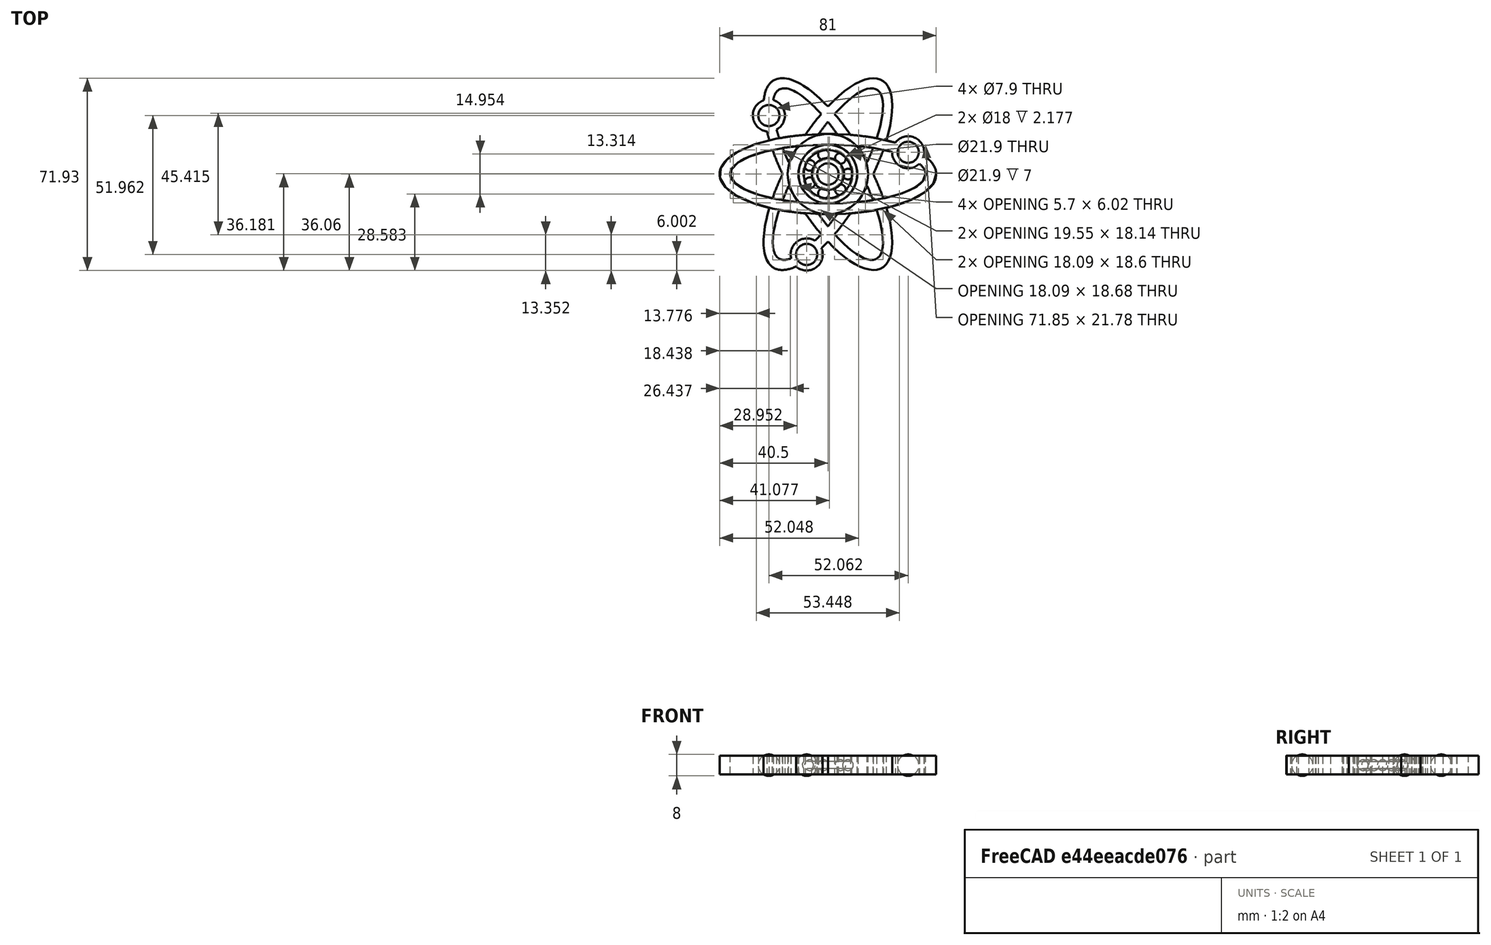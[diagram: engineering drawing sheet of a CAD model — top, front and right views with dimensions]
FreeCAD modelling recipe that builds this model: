
FCSTD DOCUMENT  (FreeCAD 0.19R)
Label: spinner-v0
License: All rights reserved
LicenseURL: http://en.wikipedia.org/wiki/All_rights_reserved
objects: Part::Cut×5, App::DocumentObjectGroup×4, Part::Sphere×4, Part::Cylinder×4, Part::Extrusion×3, Part::Feature×3, Part::MultiFuse×2, Sketcher::SketchObject×2, PartDesign::Pad×2, Mesh::Feature×2, Part::Torus×1, Part::FeaturePython×1
note: 29 computed .brp shape members not serialized (recipe doc carries the construction recipe); baked Part::Feature solids carry a one-line shape summary decoded from their .brp

FEATURE [Part::Extrusion] Extrude
  Dir = (0,0,1)
  DirMode = 2
  FaceMakerClass = Part::FaceMakerBullseye
  LengthFwd = 7
  LengthRev = 0
  Solid = true
  Symmetric = false
FEATURE [Part::Extrusion] Extrude001
  Dir = (0,0,1)
  DirMode = 2
  FaceMakerClass = Part::FaceMakerBullseye
  LengthFwd = 7
  LengthRev = 0
  Solid = true
  Symmetric = false
FEATURE [Part::Extrusion] Extrude002
  Dir = (0,0,1)
  DirMode = 2
  FaceMakerClass = Part::FaceMakerBullseye
  LengthFwd = 7
  LengthRev = 0
  Solid = true
  Symmetric = false
FEATURE [Part::MultiFuse] Fusion
  Shapes = -> [Extrude001,Extrude]
FEATURE [Part::Cut] Cut  label="ellipsis"
  Base = -> Fusion
  Refine = true
  Tool = -> Extrude002
FEATURE [Part::Feature] Cut001
  Placement = pos=(0,0,0) rot=(0,0,1;2.0944rad)
  shape: bbox 52.13 x 71.74 x 7 mm, 9 faces (baked)
FEATURE [Part::Feature] Cut002
  Placement = pos=(0,0,0) rot=(0,0,1;4.18879rad)
  shape: bbox 48.13 x 71.93 x 7 mm, 9 faces (baked)
FEATURE [Part::Feature] Cut003
  shape: bbox 81 x 30.02 x 7 mm, 9 faces (baked)
FEATURE [Sketcher::SketchObject] Sketch004
  MapMode = 5
  sketch-geometry (19):
    g0: Circle [constr] CenterX=0 CenterY=0 CenterZ=0 NormalX=0 NormalY=0 NormalZ=1 AngleXU=0 Radius=36.5
    g1: Circle [constr] CenterX=0 CenterY=0 CenterZ=0 NormalX=0 NormalY=0 NormalZ=1 AngleXU=0 Radius=40.5
    g2: Circle CenterX=0 CenterY=0 CenterZ=0 NormalX=0 NormalY=0 NormalZ=1 AngleXU=0 Radius=15
    g3: LineSegment [constr] StartX=30 StartY=6.24838 StartZ=0 EndX=30 EndY=10.0608 EndZ=0
    g4: Ellipse [constr] CenterX=0 CenterY=0 CenterZ=0 NormalX=0 NormalY=0 NormalZ=1 MajorRadius=40.5 MinorRadius=15.0095 AngleXU=0
    g5: LineSegment [constr] StartX=40.5 StartY=0 StartZ=0 EndX=-40.5 EndY=0 EndZ=0
    g6: LineSegment [constr] StartX=0 StartY=15.0095 StartZ=0 EndX=0 EndY=-15.0095 EndZ=0
    g7: GeomPoint X=37.616 Y=0 Z=0
    g8: GeomPoint X=-37.616 Y=0 Z=0
    g9: GeomPoint X=15 Y=0 Z=0
    g10: Circle CenterX=0 CenterY=0 CenterZ=0 NormalX=0 NormalY=0 NormalZ=1 AngleXU=0 Radius=10.95
    g11: Ellipse [constr] CenterX=0 CenterY=0 CenterZ=0 NormalX=0 NormalY=0 NormalZ=1 MajorRadius=36.5 MinorRadius=11.0187 AngleXU=0
    g12: LineSegment [constr] StartX=36.5 StartY=0 StartZ=0 EndX=-36.5 EndY=0 EndZ=0
    g13: LineSegment [constr] StartX=0 StartY=11.0187 StartZ=0 EndX=0 EndY=-11.0187 EndZ=0
    g14: GeomPoint X=-34.7971 Y=0 Z=0
    g15: GeomPoint X=30 Y=8.1546 Z=0
    g16: Circle [constr] CenterX=30 CenterY=8.1546 CenterZ=0 NormalX=0 NormalY=0 NormalZ=1 AngleXU=0 Radius=1.90622
    g17: Circle [constr] CenterX=30 CenterY=8.1546 CenterZ=0 NormalX=0 NormalY=0 NormalZ=1 AngleXU=0 Radius=4
    g18: Circle [constr] CenterX=30 CenterY=8.1546 CenterZ=0 NormalX=0 NormalY=0 NormalZ=1 AngleXU=0 Radius=6
  constraints (23):
    c: Coincident(g0,g-1)
    c: Diameter(g0) = 73
    c: Coincident(g1,g-1)
    c: Diameter(g1) = 81
    c: Coincident(g2,g-1)
    c: Diameter(g2) = 30
    c: Vertical(g3)
    c: DistanceX(g-1,g3) = 30
    c: InternalAlignment(g5-g8 -> g4) x4
    c: Coincident(g4,g-1)
    c: Coincident(g10,g4)
    c: InternalAlignment(g12,g11)
    c: InternalAlignment(g13,g11)
    c: InternalAlignment(g14,g11)
    c: Coincident(g11,g4)
    c: Symmetric(g3,g3,g15)
    c: Coincident(g16,g15)
    c: PointOnObject(g3,g16)
    c: Coincident(g17,g15)
    c: Diameter(g17) = 8
    c: Coincident(g18,g15)
    c: Diameter(g18) = 12
    c: Diameter(g10) = 21.9
FEATURE [PartDesign::Pad] Pad001  label="circle"
  AllowMultiFace = false
  Length = 7
  Length2 = 100
  Profile = -> Sketch004
  Type = 0
FEATURE [App::DocumentObjectGroup] Group001  label="base-components"
  Group = -> [Pad001,Cut]
FEATURE [Sketcher::SketchObject] Sketch005
  MapMode = 5
  sketch-geometry (19):
    g0: Circle [constr] CenterX=0 CenterY=0 CenterZ=0 NormalX=0 NormalY=0 NormalZ=1 AngleXU=0 Radius=36.5
    g1: Circle [constr] CenterX=0 CenterY=0 CenterZ=0 NormalX=0 NormalY=0 NormalZ=1 AngleXU=0 Radius=40.5
    g2: Circle CenterX=0 CenterY=0 CenterZ=0 NormalX=0 NormalY=0 NormalZ=1 AngleXU=0 Radius=15
    g3: LineSegment [constr] StartX=30 StartY=6.24838 StartZ=0 EndX=30 EndY=10.0608 EndZ=0
    g4: Ellipse [constr] CenterX=0 CenterY=0 CenterZ=0 NormalX=0 NormalY=0 NormalZ=1 MajorRadius=40.5 MinorRadius=15.0095 AngleXU=0
    g5: LineSegment [constr] StartX=40.5 StartY=0 StartZ=0 EndX=-40.5 EndY=0 EndZ=0
    g6: LineSegment [constr] StartX=0 StartY=15.0095 StartZ=0 EndX=0 EndY=-15.0095 EndZ=0
    g7: GeomPoint X=37.616 Y=0 Z=0
    g8: GeomPoint X=-37.616 Y=0 Z=0
    g9: GeomPoint X=15 Y=0 Z=0
    g10: Circle CenterX=0 CenterY=0 CenterZ=0 NormalX=0 NormalY=0 NormalZ=1 AngleXU=0 Radius=10.95
    g11: Ellipse [constr] CenterX=0 CenterY=0 CenterZ=0 NormalX=0 NormalY=0 NormalZ=1 MajorRadius=36.5 MinorRadius=11.0187 AngleXU=0
    g12: LineSegment [constr] StartX=36.5 StartY=0 StartZ=0 EndX=-36.5 EndY=0 EndZ=0
    g13: LineSegment [constr] StartX=0 StartY=11.0187 StartZ=0 EndX=0 EndY=-11.0187 EndZ=0
    g14: GeomPoint X=-34.7971 Y=0 Z=0
    g15: GeomPoint X=30 Y=8.1546 Z=0
    g16: Circle [constr] CenterX=30 CenterY=8.1546 CenterZ=0 NormalX=0 NormalY=0 NormalZ=1 AngleXU=0 Radius=1.90622
    g17: Circle [constr] CenterX=30 CenterY=8.1546 CenterZ=0 NormalX=0 NormalY=0 NormalZ=1 AngleXU=0 Radius=4
    g18: Circle [constr] CenterX=30 CenterY=8.1546 CenterZ=0 NormalX=0 NormalY=0 NormalZ=1 AngleXU=0 Radius=6
  constraints (23):
    c: Coincident(g0,g-1)
    c: Diameter(g0) = 73
    c: Coincident(g1,g-1)
    c: Diameter(g1) = 81
    c: Coincident(g2,g-1)
    c: Diameter(g2) = 30
    c: Vertical(g3)
    c: DistanceX(g-1,g3) = 30
    c: InternalAlignment(g5-g8 -> g4) x4
    c: Coincident(g4,g-1)
    c: Coincident(g10,g4)
    c: InternalAlignment(g12,g11)
    c: InternalAlignment(g13,g11)
    c: InternalAlignment(g14,g11)
    c: Coincident(g11,g4)
    c: Symmetric(g3,g3,g15)
    c: Coincident(g16,g15)
    c: PointOnObject(g3,g16)
    c: Coincident(g17,g15)
    c: Diameter(g17) = 8
    c: Coincident(g18,g15)
    c: Diameter(g18) = 12
    c: Diameter(g10) = 21.9
FEATURE [PartDesign::Pad] Pad002  label="circle001"
  AllowMultiFace = false
  Length = 7
  Length2 = 100
  Profile = -> Sketch005
  Type = 0
FEATURE [Part::MultiFuse] Fusion001  label="spinner"
  Refine = true
  Shapes = -> [Cut001,Cut002,Cut003,Pad002]
FEATURE [Part::Sphere] Sphere
  Angle1 = -90
  Angle2 = 90
  Angle3 = 360
  AttacherType = Attacher::AttachEngine3D
  Placement = pos=(30,8.1546,3.5) rot=(0,0,1;3.14159rad)
  Radius = 4
FEATURE [Part::Sphere] Sphere001
  Angle1 = -90
  Angle2 = 90
  Angle3 = 360
  AttacherType = Attacher::AttachEngine3D
  Placement = pos=(-7.93791,-30.0581,3.5) rot=(0,0,1;1.0472rad)
  Radius = 4
FEATURE [Part::Sphere] Sphere002
  Angle1 = -90
  Angle2 = 90
  Angle3 = 360
  AttacherType = Attacher::AttachEngine3D
  Placement = pos=(-22.0621,21.9035,3.5) rot=(0,0,-1;1.0472rad)
  Radius = 4
FEATURE [App::DocumentObjectGroup] Group  label="balls"
  Group = -> [Sphere,Sphere001,Sphere002]
FEATURE [Mesh::Feature] Mesh  label="spinner (Meshed)"
FEATURE [Mesh::Feature] Mesh001  label="Sphere (Meshed)"
FEATURE [App::DocumentObjectGroup] Group002  label="export"
  Group = -> [Mesh,Mesh001]
FEATURE [Part::Cylinder] Cylinder
  Angle = 360
  AttacherType = Attacher::AttachEngine3D
  Height = 7
  Radius = 11
FEATURE [Part::Cylinder] Cylinder001
  Angle = 360
  AttacherType = Attacher::AttachEngine3D
  Height = 7
  Radius = 4
FEATURE [Part::Cylinder] Cylinder002
  Angle = 360
  AttacherType = Attacher::AttachEngine3D
  Height = 7
  Radius = 9
FEATURE [Part::Cut] Cut004
  Base = -> Cylinder
  Tool = -> Cylinder001
FEATURE [Part::Cylinder] Cylinder003
  Angle = 360
  AttacherType = Attacher::AttachEngine3D
  Height = 7
  Radius = 6
FEATURE [Part::Cut] Cut005
  Base = -> Cylinder002
  Tool = -> Cylinder003
FEATURE [Part::Cut] Cut006
  Base = -> Cut004
  Tool = -> Cut005
FEATURE [Part::Torus] Torus
  Angle1 = -180
  Angle2 = 180
  Angle3 = 360
  AttacherType = Attacher::AttachEngine3D
  Placement = pos=(0,0,3.5) rot=(0,0,1;0rad)
  Radius1 = 7.5
  Radius2 = 2
FEATURE [Part::Cut] Cut007
  Base = -> Cut006
  Tool = -> Torus
FEATURE [Part::Sphere] Sphere003
  Angle1 = -90
  Angle2 = 90
  Angle3 = 360
  AttacherType = Attacher::AttachEngine3D
  Placement = pos=(7.5,0,3.5) rot=(0,0,1;0rad)
  Radius = 2
FEATURE [Part::FeaturePython] Array  # Draft array (typed FeaturePython)
  Angle = 360
  ArrayType = 1
  Axis = (0,0,1)
  Base = -> Sphere003
  Center = (0,0,0)
  Fuse = false
  IntervalAxis = (0,0,0)
  IntervalX = (1,0,0)
  IntervalY = (0,1,0)
  IntervalZ = (0,0,1)
  NumberPolar = 7
  NumberX = 2
  NumberY = 2
  NumberZ = 1
FEATURE [App::DocumentObjectGroup] Group003  label="bearing002"
  Group = -> [Cut007,Array]
